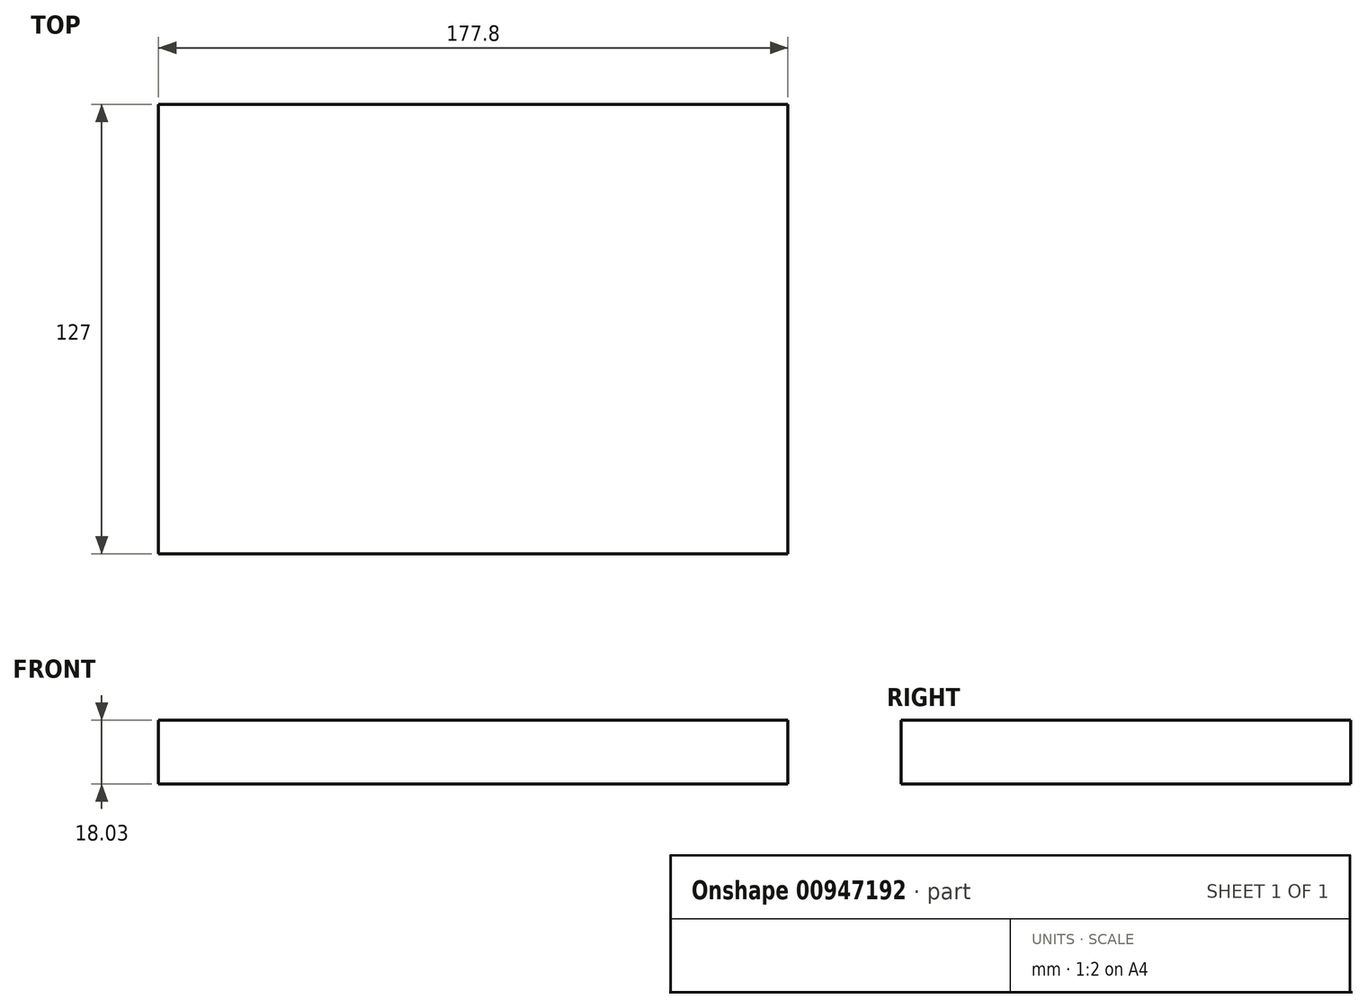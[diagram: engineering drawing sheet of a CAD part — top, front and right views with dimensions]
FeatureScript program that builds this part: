
annotation { "Feature Type Name" : "Feature", "Feature Type Description" : "" }
export const myFeature = defineFeature(function(context is Context, id is Id, definition is map)
    precondition{}
    {
        {
            var Q0;
            Q0=qCreatedBy(makeId("Top.planeOp"),FACE);
            var sketch = newSketch(context, id + "F0", { "sketchPlane" : qUnion([Q0])});
            skLineSegment(sketch, "E0.bottom", {"start": v(0, 0) * mm, "end": v(177.8, 0) * mm});
            skLineSegment(sketch, "E0.top", {"start": v(0, 127) * mm, "end": v(177.8, 127) * mm});
            skLineSegment(sketch, "E0.left", {"start": v(0, 0) * mm, "end": v(0, 127) * mm});
            skLineSegment(sketch, "E0.right", {"start": v(177.8, 0) * mm, "end": v(177.8, 127) * mm});
            skSolve(sketch);
        }
        {
            var Q0;
            Q0 = qSketchRegion(id + "F0", true);
            extrude(context, id + "F1", {"entities" : qUnion([Q0]), "depth" : 18.03 * mm, "offsetDistance" : 25.4 * mm});
        }
    });
